# Revit family: STL23775_30_40
name_source: partatom
category: Luminárias
units: mm (PartAtom-declared; Revit-internal decimal feet)

## family parameters
Compartilhado = Não
Corte com vazios quando carregada = Não
Cota do conector redondo = Utilizar diâmetro
Fonte luminosa = Não
Hospedeiro = Parede
Manter orientação da anotação = Não
Número OmniClass = 23.80.70.00
Ponto de cálculo do ambiente = Não
Sempre na vertical = Sim
Tipo de parte = Normal
Título OmniClass = Lighting

## types (2) — shared parameters
Altura = 0.7 m
Comprimento = 0.05 m
Cromado = Cromado
Dimerização = Não dimerizável
Estrutura = Al - Branco
Fabricante = Stella
Grau de proteção (IP) = IP65
IRC (Índice de reprodução de cores) = >80
Largura = 0.04 m
Modelo = Ice Long
Potência = 8 W
Tensão Elétrica = 100V-240V
URL = https://stella.com.br
Ângulo de Abertura = 110°
zero-valued in all types: Elevação padrão

## per-type parameters (varying)
| type | Fluxo Luminoso | Luminoso | Referência | Temperatura da cor (K) |
| STL23775/30 - BRANCO - BIVOLT - 3000K - 1050lm - 110° | 1050 lm | Emissivo 3000K | STL23775/30 - BIVOLT | 3000 K |
| STL23775/40 - BRANCO - BIVOLT - 4000K - 1120lm - 110° | 1120 lm | Emissivo 4000K | STL23775/40 - BIVOLT | 4000 K |
